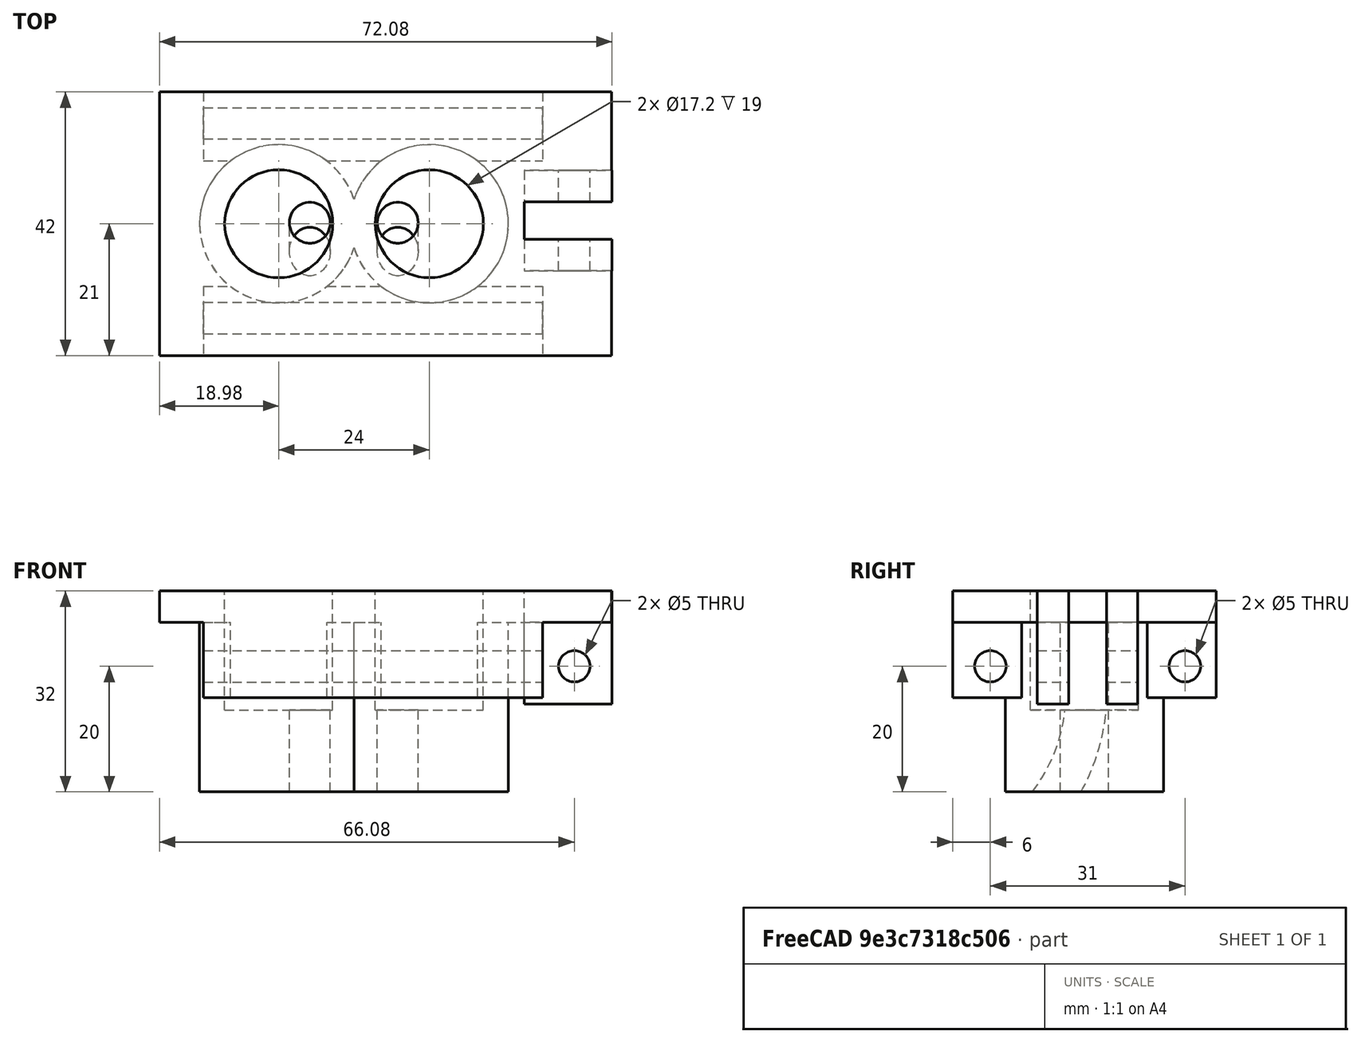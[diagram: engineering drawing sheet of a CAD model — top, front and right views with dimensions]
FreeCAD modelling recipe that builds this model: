
FCSTD DOCUMENT  (FreeCAD 0.18R16110 (Git))
Label: slider
License: All rights reserved
LicenseURL: http://en.wikipedia.org/wiki/All_rights_reserved
objects: Part::Cut×8, Part::Cylinder×7, Part::Box×6, Part::MultiFuse×3, Sketcher::SketchObject×2, Part::Sweep×2, Mesh::Feature×1
note: 28 computed .brp shape members not serialized (recipe doc carries the construction recipe); baked Part::Feature solids carry a one-line shape summary decoded from their .brp

FEATURE [Sketcher::SketchObject] Sketch028  label="Pfad"
  sketch-geometry (3):
    g0: LineSegment [constr] StartX=0 StartY=0 StartZ=0 EndX=0 EndY=30.0001 EndZ=0
    g1: LineSegment [constr] StartX=0 StartY=30.0001 StartZ=0 EndX=-30 EndY=30.0001 EndZ=0
    g2: ArcOfCircle CenterX=0 CenterY=30 CenterZ=0 NormalX=0 NormalY=0 NormalZ=1 AngleXU=0 Radius=30 StartAngle=3.14159 EndAngle=4.71239
  constraints (8):
    c: Coincident(g0,g-1)
    c: Vertical(g0)
    c: Coincident(g1,g0)
    c: Horizontal(g1)
    c: Radius(g2) = 30
    c: Tangent(g2,g-1) = -1.5708
    c: Coincident(g1,g2)
    c: DistanceX(g1,g1) = 30
FEATURE [Sketcher::SketchObject] Sketch027
  Placement = pos=(0,0,0) rot=(0.57735,0.57735,0.57735;2.0944rad)
  expr: Constraints[0] = 6.5 / 2
  sketch-geometry (1):
    g0: Circle CenterX=0.271305 CenterY=-0.135652 CenterZ=0 NormalX=0 NormalY=0 NormalZ=1 AngleXU=0 Radius=3.25
  constraints (1):
    c: Radius(g0) = 3.25
FEATURE [Part::Cylinder] Cylinder087  label="Zylinder071"
  Angle = 360
  AttacherType = Attacher::AttachEngine3D
  Height = 32
  Placement = pos=(-20,21,-32.1) rot=(0,1,0;1.5708rad)
  Radius = 12.6
FEATURE [Part::Cylinder] Cylinder107  label="Führung_li006"
  Angle = 360
  AttacherType = Attacher::AttachEngine3D
  Height = 90
  Placement = pos=(0,36,-71) rot=(1,0,0;0rad)
  Radius = 2.5
FEATURE [Part::Cylinder] Cylinder106  label="Führung_re006"
  Angle = 360
  AttacherType = Attacher::AttachEngine3D
  Height = 90
  Placement = pos=(0,5,-71) rot=(1,0,0;0rad)
  Radius = 2.5
FEATURE [Part::Cylinder] Cylinder089  label="Zylinder073"
  Angle = 360
  AttacherType = Attacher::AttachEngine3D
  Height = 22
  Placement = pos=(-7,21,-32.1) rot=(0,1,0;1.5708rad)
  Radius = 8.6
FEATURE [Part::Cylinder] Cylinder086  label="Achse_Platte001"
  Angle = 360
  AttacherType = Attacher::AttachEngine3D
  Height = 16
  Placement = pos=(0,28.5,15) rot=(1,0,0;1.5708rad)
  Radius = 2.5
FEATURE [Part::Box] Box017  label="Quader011"
  AttacherType = Attacher::AttachEngine3D
  Height = 14
  Length = 18
  Placement = pos=(-6,23.5,7) rot=(0,0,1;0rad)
  Width = 5
FEATURE [Part::Box] Box016  label="Quader010"
  AttacherType = Attacher::AttachEngine3D
  Height = 14
  Length = 18
  Placement = pos=(-6,12.5,7) rot=(0,0,1;0rad)
  Width = 5
FEATURE [Part::Box] Box014  label="Quader008"
  AttacherType = Attacher::AttachEngine3D
  Height = 14
  Length = 22
  Placement = pos=(-9,17.5,7) rot=(0,0,1;0rad)
  Width = 6
FEATURE [Part::Box] Box005  label="Quader"
  AttacherType = Attacher::AttachEngine3D
  Height = 5
  Length = 72
  Placement = pos=(7,42,-51) rot=(0.707107,0,0.707107;3.14159rad)
  Width = 42
FEATURE [Part::Cylinder] Cylinder088  label="Zylinder072"
  Angle = 360
  AttacherType = Attacher::AttachEngine3D
  Height = 32
  Placement = pos=(-20,21,-8.1) rot=(0,1,0;1.5708rad)
  Radius = 12.6
FEATURE [Part::Box] Box013  label="Schlitten002"
  AttacherType = Attacher::AttachEngine3D
  Height = 54
  Length = 12
  Placement = pos=(-5,31,-44) rot=(0,0,1;0rad)
  Width = 11
FEATURE [Part::Sweep] Sweep006
  Frenet = false
  Placement = pos=(0,20.4,-27) rot=(0,0,1;0rad)
  Sections = -> [Sketch027]
  Solid = true
  Spine = -> Sketch028 [Edge1]
  Transition = 1
FEATURE [Part::Sweep] Sweep007
  Frenet = false
  Placement = pos=(0,20.4,-13) rot=(0,0,1;0rad)
  Sections = -> [Sketch027]
  Solid = true
  Spine = -> Sketch028 [Edge1]
  Transition = 1
FEATURE [Part::Box] Box010  label="Schlitten001"
  AttacherType = Attacher::AttachEngine3D
  Height = 54
  Length = 12
  Placement = pos=(-5,0,-44) rot=(0,0,1;0rad)
  Width = 11
FEATURE [Part::MultiFuse] Fusion006  label="Schlitten"
  Placement = pos=(0,0,-0.07885) rot=(0,0,1;0rad)
  Shapes = -> [Box013,Box005,Box010]
FEATURE [Part::Cut] Cut
  Base = -> Fusion006
  Tool = -> Box014
FEATURE [Part::MultiFuse] Fusion004
  Shapes = -> [Box017,Box016,Cut]
FEATURE [Part::Cut] Cut098
  Base = -> Fusion004
  Tool = -> Cylinder086
FEATURE [Part::MultiFuse] Fusion005
  Shapes = -> [Cylinder088,Cylinder087,Cut098]
FEATURE [Part::Cut] Cut099
  Base = -> Fusion005
  Tool = -> Cylinder089
FEATURE [Part::Cylinder] Cylinder020  label="Zylinder016"
  Angle = 360
  AttacherType = Attacher::AttachEngine3D
  Height = 22
  Placement = pos=(-7,21,-8.1) rot=(0,1,0;1.5708rad)
  Radius = 8.6
FEATURE [Part::Cut] Cut100
  Base = -> Cut099
  Tool = -> Cylinder020
FEATURE [Part::Cut] Cut133
  Base = -> Cut100
  Tool = -> Cylinder106
FEATURE [Part::Cut] Cut134
  Base = -> Cut133
  Placement = pos=(4,0,0) rot=(0,0,1;0rad)
  Tool = -> Cylinder107
FEATURE [Part::Cut] Cut142
  Base = -> Cut134
  Tool = -> Sweep006
FEATURE [Part::Cut] Cut143  label="slider"
  Base = -> Cut142
  Placement = pos=(-117,140,0) rot=(0.707107,0,0.707107;3.14159rad)
  Tool = -> Sweep007
FEATURE [Mesh::Feature] Mesh  label="slider (Meshed)"
